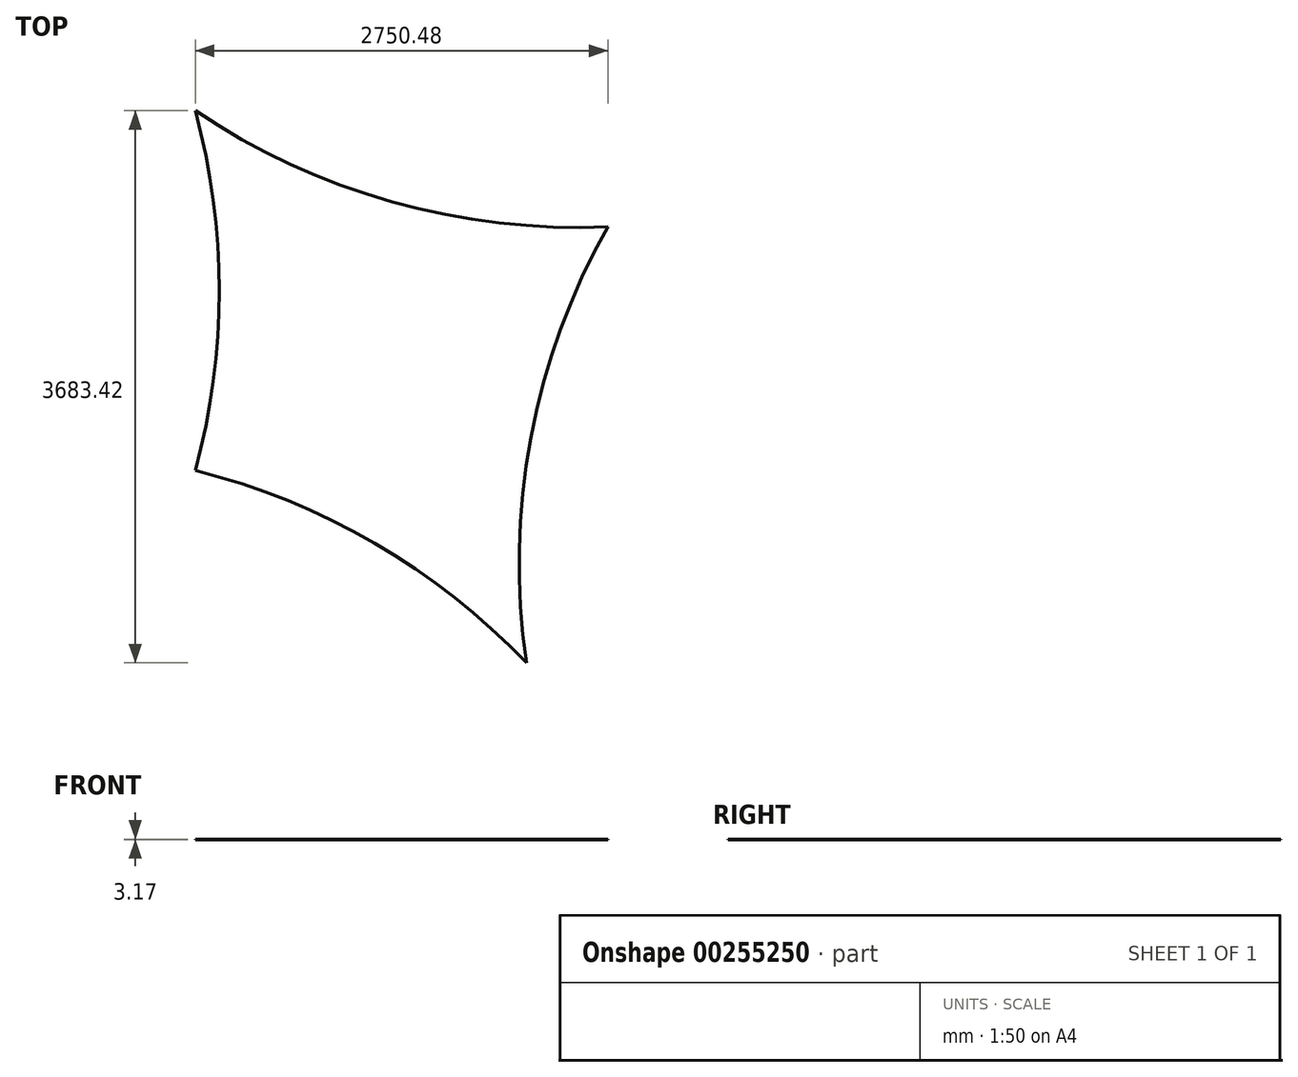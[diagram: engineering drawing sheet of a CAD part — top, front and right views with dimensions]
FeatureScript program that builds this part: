
annotation { "Feature Type Name" : "Feature", "Feature Type Description" : "" }
export const myFeature = defineFeature(function(context is Context, id is Id, definition is map)
    precondition{}
    {
        {
            var Q0;
            Q0=qCreatedBy(makeId("Top.planeOp"),FACE);
            var sketch = newSketch(context, id + "F0", { "sketchPlane" : qUnion([Q0])});
            skArc(sketch, "E0", {"start": v(0, 0) * mm, "mid": v(160.33, 1200.15) * mm, "end": v(0, 2400.3) * mm});
            skArc(sketch, "E1", {"start": v(0, 2400.3) * mm, "mid": v(1313.16, 1792.55) * mm, "end": v(2750.48, 1625.6) * mm});
            skArc(sketch, "E2", {"start": v(2750.48, 1625.6) * mm, "mid": v(2236.8, 216.44) * mm, "end": v(2206.78, -1283.12) * mm});
            skArc(sketch, "E3", {"start": v(2206.78, -1283.12) * mm, "mid": v(1194.76, -484.42) * mm, "end": v(0, 0) * mm});
            skSolve(sketch);
        }
        {
            var Q0;
            Q0 = qSketchRegion(id + "F0", true);
            extrude(context, id + "F1", {"entities" : qUnion([Q0]), "depth" : 3.17 * mm});
        }
    });
